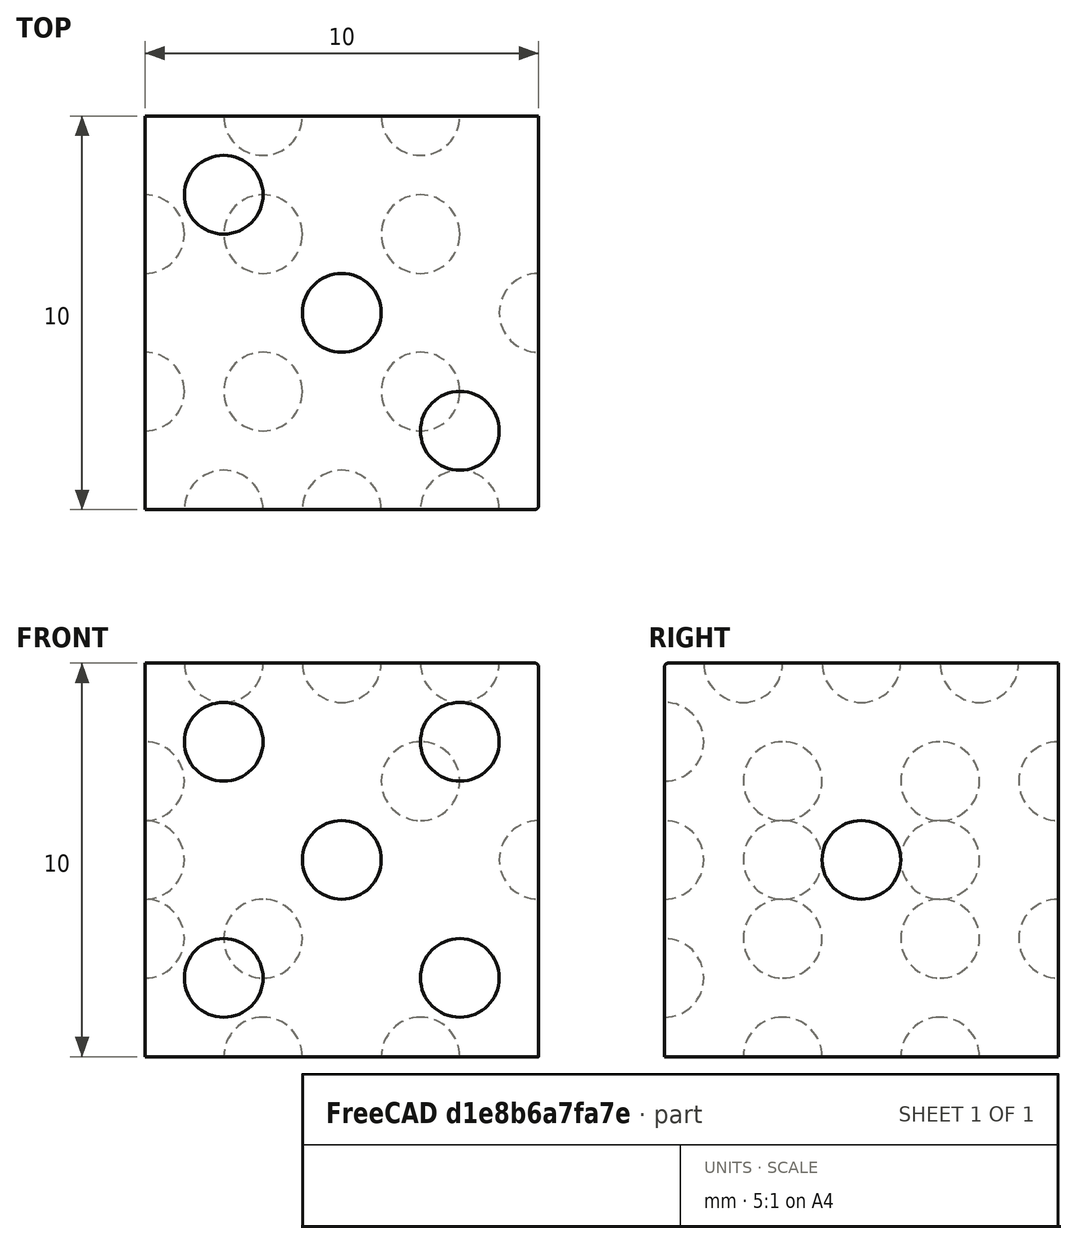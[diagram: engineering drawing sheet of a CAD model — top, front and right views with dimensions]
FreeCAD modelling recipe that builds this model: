
FCSTD DOCUMENT  (FreeCAD 0.21R33694 (Git))
Label: OJT1_T13R02_dado
License: All rights reserved
LicenseURL: http://en.wikipedia.org/wiki/All_rights_reserved
objects: Part::Sphere×21, Part::Cut×21, Part::Box×1, Part::Fillet×1
note: 44 computed .brp shape members not serialized (recipe doc carries the construction recipe); baked Part::Feature solids carry a one-line shape summary decoded from their .brp

FEATURE [Part::Box] Box  label="Cube"
  AttacherType = Attacher::AttachEngine3D
  Height = 10
  Length = 10
  Width = 10
FEATURE [Part::Sphere] Sphere
  Angle1 = -90
  Angle2 = 90
  Angle3 = 360
  AttacherType = Attacher::AttachEngine3D
  Placement = pos=(10,5,5) rot=(0,0,1;0rad)
  Radius = 1
FEATURE [Part::Sphere] Sphere001
  Angle1 = -90
  Angle2 = 90
  Angle3 = 360
  AttacherType = Attacher::AttachEngine3D
  Placement = pos=(5,5,10) rot=(0,0,1;0rad)
  Radius = 1
FEATURE [Part::Sphere] Sphere002
  Angle1 = -90
  Angle2 = 90
  Angle3 = 360
  AttacherType = Attacher::AttachEngine3D
  Placement = pos=(7,10,7) rot=(0,0,1;0rad)
  Radius = 1
FEATURE [Part::Sphere] Sphere003
  Angle1 = -90
  Angle2 = 90
  Angle3 = 360
  AttacherType = Attacher::AttachEngine3D
  Placement = pos=(8,2,10) rot=(0,0,1;0rad)
  Radius = 1
FEATURE [Part::Sphere] Sphere004
  Angle1 = -90
  Angle2 = 90
  Angle3 = 360
  AttacherType = Attacher::AttachEngine3D
  Placement = pos=(2,8,10) rot=(0,0,1;0rad)
  Radius = 1
FEATURE [Part::Sphere] Sphere005
  Angle1 = -90
  Angle2 = 90
  Angle3 = 360
  AttacherType = Attacher::AttachEngine3D
  Placement = pos=(3,10,3) rot=(0,0,1;0rad)
  Radius = 1
FEATURE [Part::Sphere] Sphere006
  Angle1 = -90
  Angle2 = 90
  Angle3 = 360
  AttacherType = Attacher::AttachEngine3D
  Placement = pos=(5,0,5) rot=(0,0,1;0rad)
  Radius = 1
FEATURE [Part::Sphere] Sphere008
  Angle1 = -90
  Angle2 = 90
  Angle3 = 360
  AttacherType = Attacher::AttachEngine3D
  Placement = pos=(8,0,8) rot=(0,0,1;0rad)
  Radius = 1
FEATURE [Part::Sphere] Sphere009
  Angle1 = -90
  Angle2 = 90
  Angle3 = 360
  AttacherType = Attacher::AttachEngine3D
  Placement = pos=(2,0,2) rot=(0,0,1;0rad)
  Radius = 1
FEATURE [Part::Sphere] Sphere010
  Angle1 = -90
  Angle2 = 90
  Angle3 = 360
  AttacherType = Attacher::AttachEngine3D
  Placement = pos=(8,0,2) rot=(0,0,1;0rad)
  Radius = 1
FEATURE [Part::Sphere] Sphere011
  Angle1 = -90
  Angle2 = 90
  Angle3 = 360
  AttacherType = Attacher::AttachEngine3D
  Placement = pos=(2,0,8) rot=(0,0,1;0rad)
  Radius = 1
FEATURE [Part::Sphere] Sphere012
  Angle1 = -90
  Angle2 = 90
  Angle3 = 360
  AttacherType = Attacher::AttachEngine3D
  Placement = pos=(7,7,0) rot=(0,0,1;0rad)
  Radius = 1
FEATURE [Part::Sphere] Sphere013
  Angle1 = -90
  Angle2 = 90
  Angle3 = 360
  AttacherType = Attacher::AttachEngine3D
  Placement = pos=(7,3,0) rot=(0,0,1;0rad)
  Radius = 1
FEATURE [Part::Sphere] Sphere014
  Angle1 = -90
  Angle2 = 90
  Angle3 = 360
  AttacherType = Attacher::AttachEngine3D
  Placement = pos=(3,7,0) rot=(0,0,1;0rad)
  Radius = 1
FEATURE [Part::Sphere] Sphere015
  Angle1 = -90
  Angle2 = 90
  Angle3 = 360
  AttacherType = Attacher::AttachEngine3D
  Placement = pos=(3,3,0) rot=(0,0,1;0rad)
  Radius = 1
FEATURE [Part::Sphere] Sphere016
  Angle1 = -90
  Angle2 = 90
  Angle3 = 360
  AttacherType = Attacher::AttachEngine3D
  Placement = pos=(0,7,7) rot=(0,0,1;0rad)
  Radius = 1
FEATURE [Part::Sphere] Sphere017
  Angle1 = -90
  Angle2 = 90
  Angle3 = 360
  AttacherType = Attacher::AttachEngine3D
  Placement = pos=(0,3,7) rot=(0,0,1;0rad)
  Radius = 1
FEATURE [Part::Sphere] Sphere018
  Angle1 = -90
  Angle2 = 90
  Angle3 = 360
  AttacherType = Attacher::AttachEngine3D
  Placement = pos=(0,7,5) rot=(0,0,1;0rad)
  Radius = 1
FEATURE [Part::Sphere] Sphere019
  Angle1 = -90
  Angle2 = 90
  Angle3 = 360
  AttacherType = Attacher::AttachEngine3D
  Placement = pos=(0,3,5) rot=(0,0,1;0rad)
  Radius = 1
FEATURE [Part::Sphere] Sphere020
  Angle1 = -90
  Angle2 = 90
  Angle3 = 360
  AttacherType = Attacher::AttachEngine3D
  Placement = pos=(0,7,3) rot=(0,0,1;0rad)
  Radius = 1
FEATURE [Part::Sphere] Sphere021
  Angle1 = -90
  Angle2 = 90
  Angle3 = 360
  AttacherType = Attacher::AttachEngine3D
  Placement = pos=(0,3,3) rot=(0,0,1;0rad)
  Radius = 1
FEATURE [Part::Cut] Cut
  Base = -> Box
  Refine = true
  Tool = -> Sphere021
FEATURE [Part::Cut] Cut001
  Base = -> Cut
  Refine = true
  Tool = -> Sphere020
FEATURE [Part::Cut] Cut002
  Base = -> Cut001
  Refine = true
  Tool = -> Sphere019
FEATURE [Part::Cut] Cut003
  Base = -> Cut002
  Refine = true
  Tool = -> Sphere018
FEATURE [Part::Cut] Cut004
  Base = -> Cut003
  Refine = true
  Tool = -> Sphere017
FEATURE [Part::Cut] Cut005
  Base = -> Cut004
  Refine = true
  Tool = -> Sphere016
FEATURE [Part::Cut] Cut006
  Base = -> Cut005
  Refine = true
  Tool = -> Sphere015
FEATURE [Part::Cut] Cut007
  Base = -> Cut006
  Refine = true
  Tool = -> Sphere014
FEATURE [Part::Cut] Cut008
  Base = -> Cut007
  Refine = true
  Tool = -> Sphere013
FEATURE [Part::Cut] Cut009
  Base = -> Cut008
  Refine = true
  Tool = -> Sphere012
FEATURE [Part::Cut] Cut010
  Base = -> Cut009
  Refine = true
  Tool = -> Sphere011
FEATURE [Part::Cut] Cut011
  Base = -> Cut010
  Refine = true
  Tool = -> Sphere010
FEATURE [Part::Cut] Cut012
  Base = -> Cut011
  Refine = true
  Tool = -> Sphere009
FEATURE [Part::Cut] Cut013
  Base = -> Cut012
  Refine = true
  Tool = -> Sphere008
FEATURE [Part::Cut] Cut014
  Base = -> Cut013
  Refine = true
  Tool = -> Sphere006
FEATURE [Part::Cut] Cut015
  Base = -> Cut014
  Refine = true
  Tool = -> Sphere005
FEATURE [Part::Cut] Cut016
  Base = -> Cut015
  Refine = true
  Tool = -> Sphere004
FEATURE [Part::Cut] Cut017
  Base = -> Cut016
  Refine = true
  Tool = -> Sphere003
FEATURE [Part::Cut] Cut018
  Base = -> Cut017
  Refine = true
  Tool = -> Sphere002
FEATURE [Part::Cut] Cut019
  Base = -> Cut018
  Refine = true
  Tool = -> Sphere001
FEATURE [Part::Cut] Cut020
  Base = -> Cut019
  Refine = true
  Tool = -> Sphere
FEATURE [Part::Fillet] Fillet
  Base = -> Cut020
  Edges = 3 edges r=0.1: [Edge18,Edge19,Edge31]
